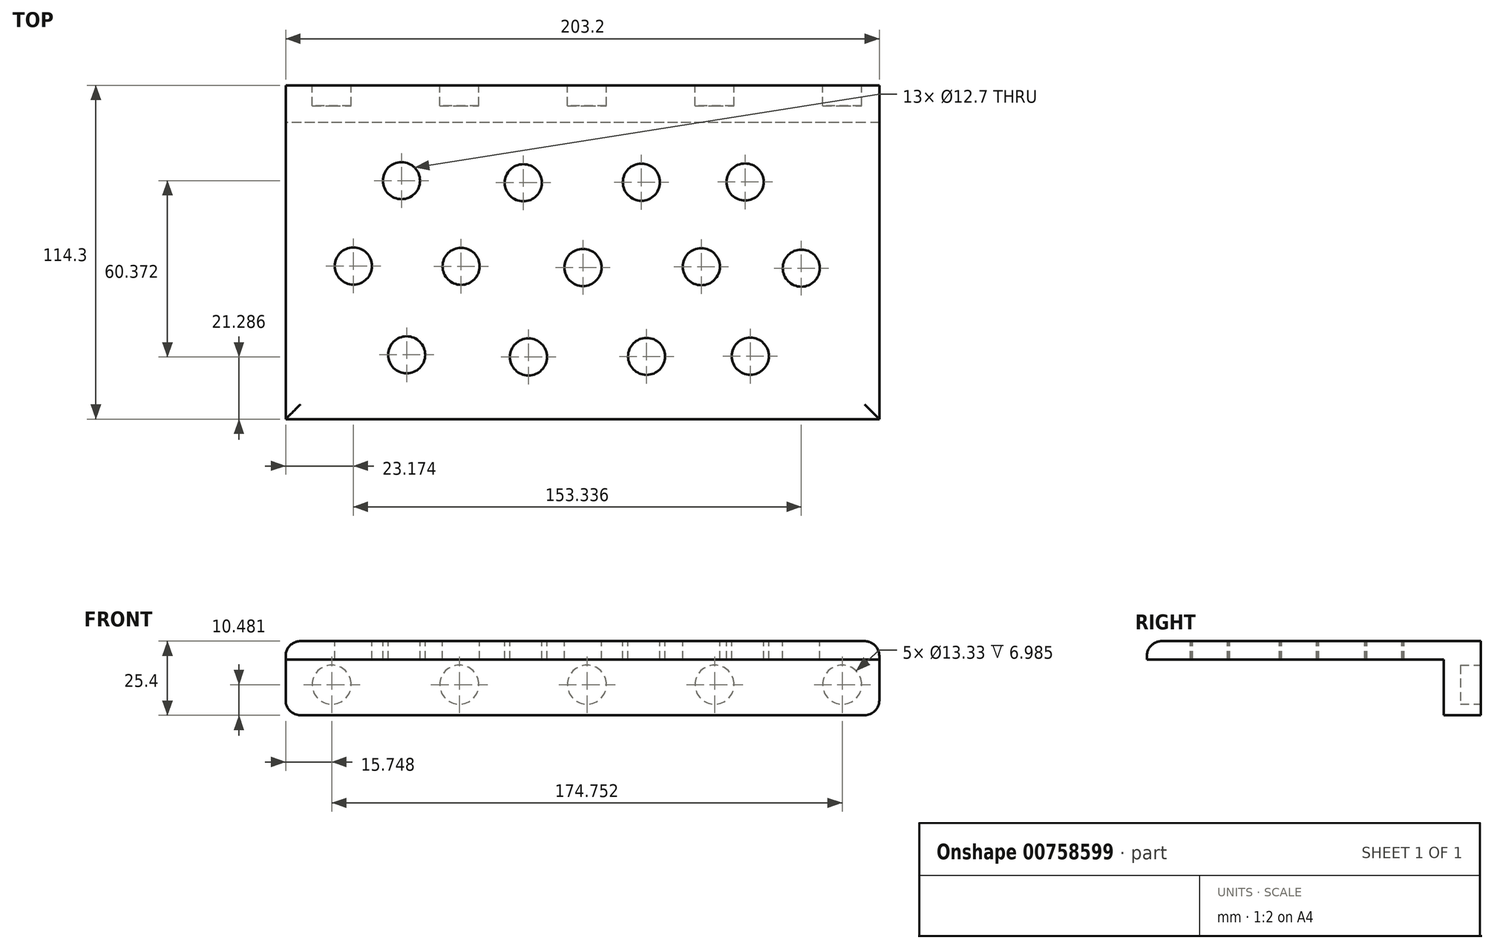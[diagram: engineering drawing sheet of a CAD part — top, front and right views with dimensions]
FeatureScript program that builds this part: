
annotation { "Feature Type Name" : "Feature", "Feature Type Description" : "" }
export const myFeature = defineFeature(function(context is Context, id is Id, definition is map)
    precondition{}
    {
        {
            var Q0;
            Q0=qCreatedBy(makeId("Top.planeOp"),FACE);
            var sketch = newSketch(context, id + "F0", { "sketchPlane" : qUnion([Q0])});
            skLineSegment(sketch, "E0.bottom", {"start": v(-101.6, 57.15) * mm, "end": v(101.6, 57.15) * mm});
            skLineSegment(sketch, "E0.top", {"start": v(-101.6, -57.15) * mm, "end": v(101.6, -57.15) * mm});
            skLineSegment(sketch, "E0.left", {"start": v(-101.6, 57.15) * mm, "end": v(-101.6, -57.15) * mm});
            skLineSegment(sketch, "E0.right", {"start": v(101.6, 57.15) * mm, "end": v(101.6, -57.15) * mm});
            skPoint(sketch, "E1", {"position": v(0, 57.15) * mm});
            skPoint(sketch, "E2", {"position": v(-101.6, 0) * mm});
            skSolve(sketch);
        }
        {
            var Q0;
            Q0 = qSketchRegion(id + "F0", true);
            extrude(context, id + "F1", {"entities" : qUnion([Q0]), "depth" : 6.35 * mm, "offsetDistance" : 25.4 * mm});
        }
        {
            var Q0;
            Q0=qCreatedBy(makeId("Right.planeOp"),FACE);
            var sketch = newSketch(context, id + "F2", { "sketchPlane" : qUnion([Q0])});
            skLineSegment(sketch, "E3.bottom", {"start": v(57.15, 0) * mm, "end": v(44.45, 0) * mm});
            skLineSegment(sketch, "E3.top", {"start": v(57.15, -19.05) * mm, "end": v(44.45, -19.05) * mm});
            skLineSegment(sketch, "E3.left", {"start": v(57.15, 0) * mm, "end": v(57.15, -19.05) * mm});
            skLineSegment(sketch, "E3.right", {"start": v(44.45, 0) * mm, "end": v(44.45, -19.05) * mm});
            skSolve(sketch);
        }
        {
            var Q0;
            Q0 = qSketchRegion(id + "F2", true);
            extrude(context, id + "F3", {"entities" : qUnion([Q0]), "operationType" : NewBodyOperationType.ADD, "depth" : 101.6 * mm, "offsetDistance" : 25.4 * mm, "hasSecondDirection" : true, "secondDirectionOppositeDirection" : true, "secondDirectionDepth" : 101.6 * mm});
        }
        {
            var Q0;
            Q0=makeQuery(id+"F1.opExtrude","CAP_EDGE",EDGE,{"disambiguationData":[OSD([sQuery(id+"F0.wireOp",EDGE,"E0.top")])],"isStart":false});
            var Q1;
            Q1=makeQuery(id+"F1.opExtrude","CAP_EDGE",EDGE,{"disambiguationData":[OSD([sQuery(id+"F0.wireOp",EDGE,"E0.left")])],"isStart":false});
            var Q2;
            Q2=makeQuery(id+"F1.opExtrude","CAP_EDGE",EDGE,{"disambiguationData":[OSD([sQuery(id+"F0.wireOp",EDGE,"E0.right")])],"isStart":false});
            fillet(context, id + "F4", {"entities" : qUnion([Q0, Q1, Q2]), "radius" : 5.08 * mm, "tangentPropagation" : true, "allowEdgeOverflow" : false});
        }
        {
            var Q0;
            Q0=makeQuery(id+"F1.opExtrude","CAP_FACE",FACE,{"disambiguationData":[OSD([sQuery(id+"F0.wireOp",EDGE,"E0.bottom"),sQuery(id+"F0.wireOp",EDGE,"E0.top"),sQuery(id+"F0.wireOp",EDGE,"E0.left"),sQuery(id+"F0.wireOp",EDGE,"E0.right")])],"isStart":false});
            var sketch = newSketch(context, id + "F5", { "sketchPlane" : qUnion([Q0])});
            skCircle(sketch, "E4", {"center": v(-61.97, 24.5) * mm, "radius": 6.35 * mm});
            skCircle(sketch, "E5", {"center": v(-20.26, 23.78) * mm, "radius": 6.35 * mm});
            skCircle(sketch, "E6", {"center": v(20.17, 23.98) * mm, "radius": 6.35 * mm});
            skCircle(sketch, "E7", {"center": v(55.66, 24.06) * mm, "radius": 6.35 * mm});
            skCircle(sketch, "E8", {"center": v(-78.43, -4.71) * mm, "radius": 6.35 * mm});
            skCircle(sketch, "E9", {"center": v(-41.55, -4.81) * mm, "radius": 6.35 * mm});
            skCircle(sketch, "E10", {"center": v(0.16, -5.21) * mm, "radius": 6.35 * mm});
            skCircle(sketch, "E11", {"center": v(40.67, -4.94) * mm, "radius": 6.35 * mm});
            skCircle(sketch, "E12", {"center": v(74.9, -5.44) * mm, "radius": 6.35 * mm});
            skCircle(sketch, "E13", {"center": v(-60.2, -35.14) * mm, "radius": 6.35 * mm});
            skCircle(sketch, "E14", {"center": v(-18.49, -35.86) * mm, "radius": 6.35 * mm});
            skCircle(sketch, "E15", {"center": v(21.94, -35.66) * mm, "radius": 6.35 * mm});
            skCircle(sketch, "E16", {"center": v(57.44, -35.59) * mm, "radius": 6.35 * mm});
            skSolve(sketch);
        }
        {
            var Q0;
            Q0=makeQuery(id+"F5.imprint","IMPRINT",FACE,{"disambiguationData":[TD([[makeQuery(id+"F5.imprint","IMPRINT",EDGE,{"derivedFrom":sQuery(id+"F5.wireOp",EDGE,"E8")}),1.0]])]});
            var Q1;
            Q1=makeQuery(id+"F5.imprint","IMPRINT",FACE,{"disambiguationData":[TD([[makeQuery(id+"F5.imprint","IMPRINT",EDGE,{"derivedFrom":sQuery(id+"F5.wireOp",EDGE,"E5")}),1.0]])]});
            var Q2;
            Q2=makeQuery(id+"F5.imprint","IMPRINT",FACE,{"disambiguationData":[TD([[makeQuery(id+"F5.imprint","IMPRINT",EDGE,{"derivedFrom":sQuery(id+"F5.wireOp",EDGE,"E4")}),1.0]])]});
            var Q3;
            Q3=makeQuery(id+"F5.imprint","IMPRINT",FACE,{"disambiguationData":[TD([[makeQuery(id+"F5.imprint","IMPRINT",EDGE,{"derivedFrom":sQuery(id+"F5.wireOp",EDGE,"E15")}),1.0]])]});
            var Q4;
            Q4=makeQuery(id+"F5.imprint","IMPRINT",FACE,{"disambiguationData":[TD([[makeQuery(id+"F5.imprint","IMPRINT",EDGE,{"derivedFrom":sQuery(id+"F5.wireOp",EDGE,"E6")}),1.0]])]});
            var Q5;
            Q5=makeQuery(id+"F5.imprint","IMPRINT",FACE,{"disambiguationData":[TD([[makeQuery(id+"F5.imprint","IMPRINT",EDGE,{"derivedFrom":sQuery(id+"F5.wireOp",EDGE,"E10")}),1.0]])]});
            var Q6;
            Q6=makeQuery(id+"F5.imprint","IMPRINT",FACE,{"disambiguationData":[TD([[makeQuery(id+"F5.imprint","IMPRINT",EDGE,{"derivedFrom":sQuery(id+"F5.wireOp",EDGE,"E7")}),1.0]])]});
            var Q7;
            Q7=makeQuery(id+"F5.imprint","IMPRINT",FACE,{"disambiguationData":[TD([[makeQuery(id+"F5.imprint","IMPRINT",EDGE,{"derivedFrom":sQuery(id+"F5.wireOp",EDGE,"E12")}),1.0]])]});
            var Q8;
            Q8=makeQuery(id+"F5.imprint","IMPRINT",FACE,{"disambiguationData":[TD([[makeQuery(id+"F5.imprint","IMPRINT",EDGE,{"derivedFrom":sQuery(id+"F5.wireOp",EDGE,"E9")}),1.0]])]});
            var Q9;
            Q9=makeQuery(id+"F5.imprint","IMPRINT",FACE,{"disambiguationData":[TD([[makeQuery(id+"F5.imprint","IMPRINT",EDGE,{"derivedFrom":sQuery(id+"F5.wireOp",EDGE,"E14")}),1.0]])]});
            var Q10;
            Q10=makeQuery(id+"F5.imprint","IMPRINT",FACE,{"disambiguationData":[TD([[makeQuery(id+"F5.imprint","IMPRINT",EDGE,{"derivedFrom":sQuery(id+"F5.wireOp",EDGE,"E11")}),1.0]])]});
            var Q11;
            Q11=makeQuery(id+"F5.imprint","IMPRINT",FACE,{"disambiguationData":[TD([[makeQuery(id+"F5.imprint","IMPRINT",EDGE,{"derivedFrom":sQuery(id+"F5.wireOp",EDGE,"E13")}),1.0]])]});
            var Q12;
            Q12=makeQuery(id+"F5.imprint","IMPRINT",FACE,{"disambiguationData":[TD([[makeQuery(id+"F5.imprint","IMPRINT",EDGE,{"derivedFrom":sQuery(id+"F5.wireOp",EDGE,"E16")}),1.0]])]});
            extrude(context, id + "F6", {"entities" : qUnion([Q0, Q1, Q2, Q3, Q4, Q5, Q6, Q7, Q8, Q9, Q10, Q11, Q12]), "operationType" : NewBodyOperationType.REMOVE, "endBound" : BoundingType.THROUGH_ALL, "oppositeDirection" : true, "depth" : 25.4 * mm, "offsetDistance" : 25.4 * mm});
        }
        {
            var Q0;
            Q0=makeQuery(id+"F3.opExtrude","CAP_EDGE",EDGE,{"disambiguationData":[OSD([sQuery(id+"F2.wireOp",EDGE,"E3.top")])],"isStart":true});
            var Q1;
            Q1=makeQuery(id+"F3.opExtrude","CAP_EDGE",EDGE,{"disambiguationData":[OSD([sQuery(id+"F2.wireOp",EDGE,"E3.top")])],"isStart":false});
            fillet(context, id + "F7", {"entities" : qUnion([Q0, Q1]), "radius" : 5.08 * mm, "tangentPropagation" : true, "allowEdgeOverflow" : false});
        }
        {
            var Q0;
            Q0=makeQuery(id+"F3.opExtrude","SWEPT_FACE",FACE,{"disambiguationData":[OSD([sQuery(id+"F2.wireOp",EDGE,"E3.left")])]});
            var sketch = newSketch(context, id + "F8", { "sketchPlane" : qUnion([Q0])});
            skCircle(sketch, "E17", {"center": v(-45.21, -8.57) * mm, "radius": 6.67 * mm});
            skCircle(sketch, "E18", {"center": v(-88.9, -8.57) * mm, "radius": 6.67 * mm});
            skCircle(sketch, "E19", {"center": v(-1.52, -8.57) * mm, "radius": 6.67 * mm});
            skCircle(sketch, "E20", {"center": v(42.16, -8.57) * mm, "radius": 6.67 * mm});
            skCircle(sketch, "E21", {"center": v(85.85, -8.57) * mm, "radius": 6.67 * mm});
            skSolve(sketch);
        }
        {
            var Q0;
            Q0 = qSketchRegion(id + "F8", true);
            extrude(context, id + "F9", {"entities" : qUnion([Q0]), "operationType" : NewBodyOperationType.REMOVE, "oppositeDirection" : true, "depth" : 7 * mm, "offsetDistance" : 25.4 * mm});
        }
    });
